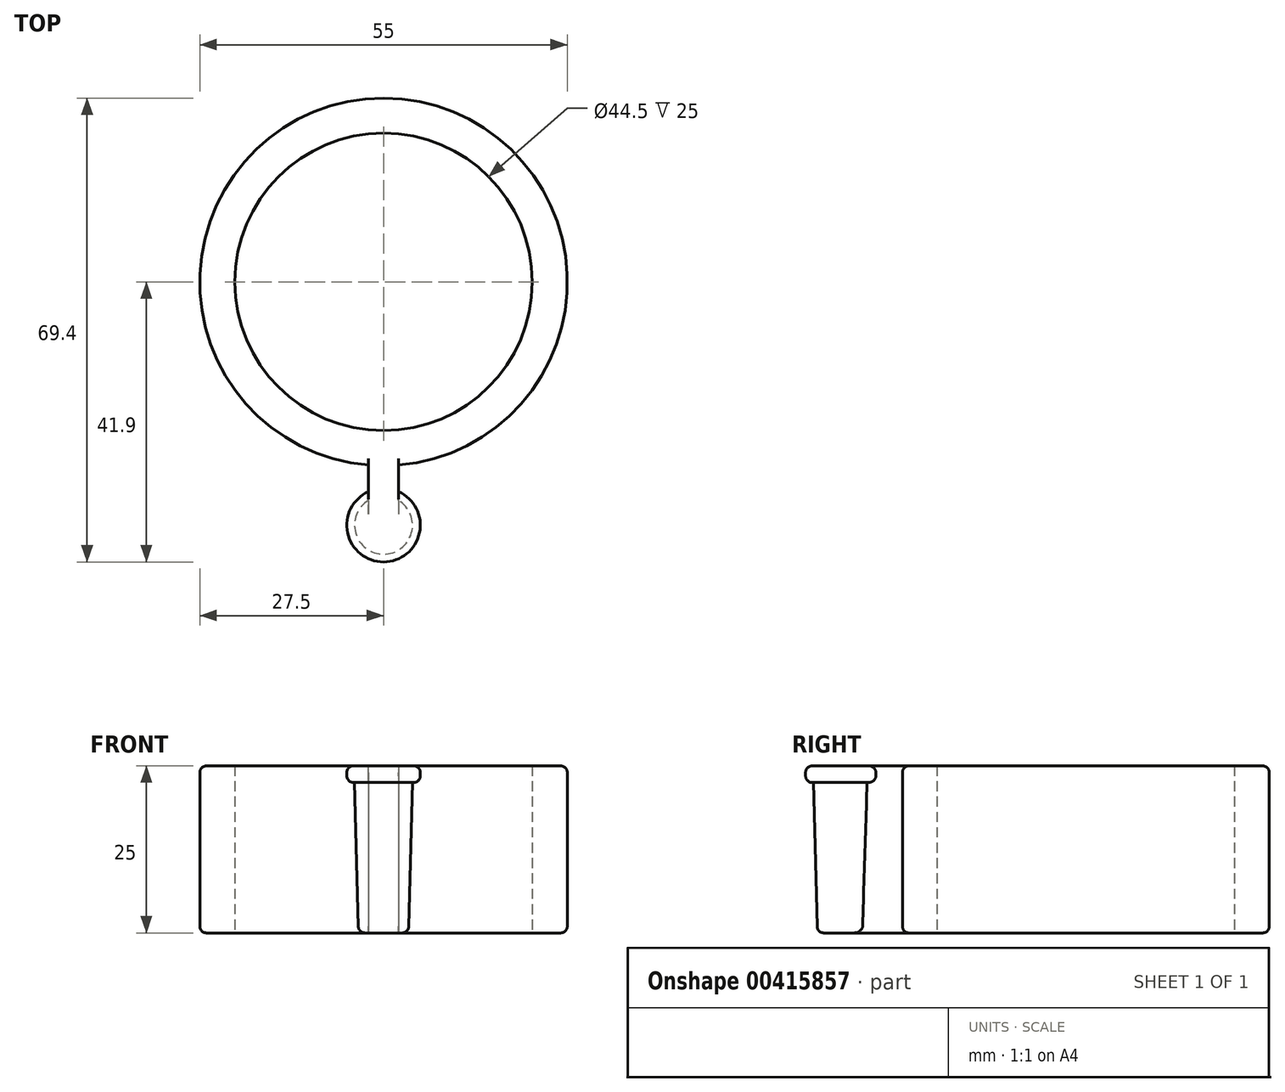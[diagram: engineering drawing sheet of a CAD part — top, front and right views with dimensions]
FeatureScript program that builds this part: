
annotation { "Feature Type Name" : "Feature", "Feature Type Description" : "" }
export const myFeature = defineFeature(function(context is Context, id is Id, definition is map)
    precondition{}
    {
        {
            var Q0;
            Q0=qCreatedBy(makeId("Top.planeOp"),FACE);
            var sketch = newSketch(context, id + "F0", { "sketchPlane" : qUnion([Q0])});
            skCircle(sketch, "E0", {"center": v(0, 0) * mm, "radius": 27.5 * mm});
            skCircle(sketch, "E1", {"center": v(0, 0) * mm, "radius": 22.25 * mm});
            skSolve(sketch);
        }
        {
            var Q0;
            Q0=makeQuery(id+"F0.imprint","IMPRINT",FACE,{"disambiguationData":[TD([[makeQuery(id+"F0.imprint","IMPRINT",EDGE,{"derivedFrom":sQuery(id+"F0.wireOp",EDGE,"G8LjAgH3-xLvY-zyrB-EcI2-Q5GBPlgTxXza")}),-1.0]])]});
            var Q1;
            Q1=makeQuery(id+"F0.imprint","IMPRINT",FACE,{"disambiguationData":[TD([[makeQuery(id+"F0.imprint","IMPRINT",EDGE,{"derivedFrom":sQuery(id+"F0.wireOp",EDGE,"E0")}),1.0]])]});
            extrude(context, id + "F1", {"entities" : qUnion([Q0, Q1]), "depth" : 25 * mm});
        }
        {
            var Q0;
            Q0=qCreatedBy(makeId("Right.planeOp"),FACE);
            var sketch = newSketch(context, id + "F2", { "sketchPlane" : qUnion([Q0])});
            skLineSegment(sketch, "E2.0", {"start": v(-2.25, 25) * mm, "end": v(2.25, 25) * mm});
            skLineSegment(sketch, "E3", {"start": v(2.25, 25) * mm, "end": v(2.25, 0) * mm});
            skLineSegment(sketch, "E4", {"start": v(-2.25, 25) * mm, "end": v(-2.25, 0) * mm});
            skPoint(sketch, "E5.orphan", {"position": v(-27.5, 25) * mm});
            skPoint(sketch, "E6.orphan", {"position": v(27.5, 25) * mm});
            skLineSegment(sketch, "E7", {"start": v(2.25, 0) * mm, "end": v(-2.25, 0) * mm});
            skSolve(sketch);
        }
        {
            var Q0;
            Q0=qCreatedBy(makeId("Front.planeOp"),FACE);
            cPlane(context, id + "F3", {"entities" : qUnion([Q0]), "cplaneType" : CPlaneType.OFFSET, "offset" : ((55 / 2) + 8) * mm, "width" : 150 * mm, "height" : 150 * mm});
        }
        {
            var Q0;
            Q0=qCreatedBy(id+"F3.planeOp",FACE);
            var sketch = newSketch(context, id + "F4", { "sketchPlane" : qUnion([Q0])});
            skLineSegment(sketch, "E8.0", {"start": v(-2.25, 25) * mm, "end": v(2.25, 25) * mm});
            skLineSegment(sketch, "E9", {"start": v(2.25, 25) * mm, "end": v(2.25, 0) * mm});
            skLineSegment(sketch, "E10", {"start": v(-2.25, 25) * mm, "end": v(-2.25, 0) * mm});
            skPoint(sketch, "E11.orphan", {"position": v(-27.5, 25) * mm});
            skPoint(sketch, "E12.orphan", {"position": v(27.5, 25) * mm});
            skLineSegment(sketch, "E13", {"start": v(2.25, 0) * mm, "end": v(-2.25, 0) * mm});
            skSolve(sketch);
        }
        {
            var Q0;
            Q0=makeQuery(id+"F8.boolean.opBoolean","MERGE",FACE,{"derivedFrom":[makeQuery(id+"F1.opExtrude","CAP_FACE",FACE,{"disambiguationData":[OSD([sQuery(id+"F0.wireOp",EDGE,"G8LjAgH3-xLvY-zyrB-EcI2-Q5GBPlgTxXza"),sQuery(id+"F0.wireOp",EDGE,"TrwqLrFX-PL90-re9a-MtEJ-rmMyrkPkawyX"),sQuery(id+"F0.wireOp",EDGE,"UjxkqwY4-PdTA-AksG-SiQF-jZbG1BaBsUn5"),sQuery(id+"F0.wireOp",EDGE,"fVokzXBM-DoVm-PEKz-oAMV-pJyANEdUcLKx"),sQuery(id+"F0.wireOp",EDGE,"49fcca35-5327-4fc4-9edf-febdfafce598.1.0"),sQuery(id+"F0.wireOp",EDGE,"49fcca35-5327-4fc4-9edf-febdfafce598.1.1"),sQuery(id+"F0.wireOp",EDGE,"49fcca35-5327-4fc4-9edf-febdfafce598.2.0"),sQuery(id+"F0.wireOp",EDGE,"49fcca35-5327-4fc4-9edf-febdfafce598.2.1"),sQuery(id+"F0.wireOp",EDGE,"49fcca35-5327-4fc4-9edf-febdfafce598.3.0"),sQuery(id+"F0.wireOp",EDGE,"49fcca35-5327-4fc4-9edf-febdfafce598.3.1"),sQuery(id+"F0.wireOp",EDGE,"49fcca35-5327-4fc4-9edf-febdfafce598.4.0"),sQuery(id+"F0.wireOp",EDGE,"49fcca35-5327-4fc4-9edf-febdfafce598.4.1"),sQuery(id+"F0.wireOp",EDGE,"49fcca35-5327-4fc4-9edf-febdfafce598.5.0"),sQuery(id+"F0.wireOp",EDGE,"49fcca35-5327-4fc4-9edf-febdfafce598.5.1"),sQuery(id+"F0.wireOp",EDGE,"49fcca35-5327-4fc4-9edf-febdfafce598.6.0"),sQuery(id+"F0.wireOp",EDGE,"49fcca35-5327-4fc4-9edf-febdfafce598.6.1"),sQuery(id+"F0.wireOp",EDGE,"49fcca35-5327-4fc4-9edf-febdfafce598.7.0"),sQuery(id+"F0.wireOp",EDGE,"49fcca35-5327-4fc4-9edf-febdfafce598.7.1"),sQuery(id+"F0.wireOp",EDGE,"49fcca35-5327-4fc4-9edf-febdfafce598.8.0"),sQuery(id+"F0.wireOp",EDGE,"49fcca35-5327-4fc4-9edf-febdfafce598.8.1"),sQuery(id+"F0.wireOp",EDGE,"49fcca35-5327-4fc4-9edf-febdfafce598.9.0"),sQuery(id+"F0.wireOp",EDGE,"49fcca35-5327-4fc4-9edf-febdfafce598.9.1"),sQuery(id+"F0.wireOp",EDGE,"49fcca35-5327-4fc4-9edf-febdfafce598.10.0"),sQuery(id+"F0.wireOp",EDGE,"49fcca35-5327-4fc4-9edf-febdfafce598.10.1"),sQuery(id+"F0.wireOp",EDGE,"49fcca35-5327-4fc4-9edf-febdfafce598.11.0"),sQuery(id+"F0.wireOp",EDGE,"49fcca35-5327-4fc4-9edf-febdfafce598.11.1"),sQuery(id+"F0.wireOp",EDGE,"E0"),sQuery(id+"F0.wireOp",EDGE,"186aa438-9647-4cfe-b0f9-6be8f9764cad.trimOffspring"),sQuery(id+"F0.wireOp",EDGE,"58acbb79-e031-4346-80cd-8f142c05cd66.trimOffspring"),sQuery(id+"F0.wireOp",EDGE,"3233a842-d643-44c9-9bbf-ea4239158afc.trimOffspring"),sQuery(id+"F0.wireOp",EDGE,"f7f68b4e-f9ab-4057-8afc-ee08b94aada7.trimOffspring"),sQuery(id+"F0.wireOp",EDGE,"09b310b1-5268-4a26-a1f0-9bfda1f777f2.trimOffspring"),sQuery(id+"F0.wireOp",EDGE,"060726c4-0cf8-4064-904b-376d507987ac.trimOffspring"),sQuery(id+"F0.wireOp",EDGE,"7db7c674-86fd-48a5-aafa-5ef47b045ad1.trimOffspring"),sQuery(id+"F0.wireOp",EDGE,"ee3f2828-a48d-4b0c-ae87-b5a3684aa839.trimOffspring"),sQuery(id+"F0.wireOp",EDGE,"121f7678-b1ac-4d92-82c7-cca3d9a6b96b.trimOffspring"),sQuery(id+"F0.wireOp",EDGE,"3299b9a4-9380-4aca-859c-d639b934480d.trimOffspring"),sQuery(id+"F0.wireOp",EDGE,"b3303ed2-3daa-417e-bc2a-0f817123942c.trimOffspring"),sQuery(id+"F0.wireOp",EDGE,"a895326a-27a2-4a7e-8581-99855a22d4ec.trimOffspring"),sQuery(id+"F0.wireOp",EDGE,"c02cc152-68c9-4426-bdff-746dfd7627e0.trimOffspring"),sQuery(id+"F0.wireOp",EDGE,"6c8ed3d3-5cf9-4a29-b357-0998a04bb589.trimOffspring"),sQuery(id+"F0.wireOp",EDGE,"684efb0c-3531-44ac-83f3-1a78a4206dcb.trimOffspring"),sQuery(id+"F0.wireOp",EDGE,"eba51431-7082-4955-99c3-f2a0537aa775.trimOffspring"),sQuery(id+"F0.wireOp",EDGE,"16738435-4d55-46a7-bca6-1884286cbfd4.trimOffspring"),sQuery(id+"F0.wireOp",EDGE,"9c81e3d0-4d59-40e4-9b67-e092ea49d70e.trimOffspring"),sQuery(id+"F0.wireOp",EDGE,"baf1dc81-3dee-4657-96dd-312042d0ee18.trimOffspring"),sQuery(id+"F0.wireOp",EDGE,"007a2b50-8cc2-4d21-b63f-0f999ab53aaa.trimOffspring"),sQuery(id+"F0.wireOp",EDGE,"d51a5eac-9464-4b9c-9b0a-bc628fde9c98.trimOffspring"),sQuery(id+"F0.wireOp",EDGE,"2bc9f3e7-df2b-4828-93b8-591f512d2fb0.trimOffspring")])],"isStart":false}),makeQuery(id+"F8.opExtrude","SWEPT_FACE",FACE,{"disambiguationData":[OSD([sQuery(id+"F4.wireOp",EDGE,"E8.0")])]})]});
            var sketch = newSketch(context, id + "F5", { "sketchPlane" : qUnion([Q0])});
            skCircle(sketch, "E14", {"center": v(0, -36.4) * mm, "radius": 4.4 * mm});
            skPoint(sketch, "E14.first.point", {"position": v(0, -32) * mm});
            skPoint(sketch, "E14.second.point", {"position": v(-3.9, -38.43) * mm});
            skPoint(sketch, "E14.third.point", {"position": v(2.2, -40.2) * mm});
            skSolve(sketch);
        }
        {
            var Q0;
            Q0=makeQuery(id+"F8.boolean.opBoolean","MERGE",FACE,{"derivedFrom":[makeQuery(id+"F1.opExtrude","CAP_FACE",FACE,{"disambiguationData":[OSD([sQuery(id+"F0.wireOp",EDGE,"G8LjAgH3-xLvY-zyrB-EcI2-Q5GBPlgTxXza"),sQuery(id+"F0.wireOp",EDGE,"TrwqLrFX-PL90-re9a-MtEJ-rmMyrkPkawyX"),sQuery(id+"F0.wireOp",EDGE,"UjxkqwY4-PdTA-AksG-SiQF-jZbG1BaBsUn5"),sQuery(id+"F0.wireOp",EDGE,"fVokzXBM-DoVm-PEKz-oAMV-pJyANEdUcLKx"),sQuery(id+"F0.wireOp",EDGE,"49fcca35-5327-4fc4-9edf-febdfafce598.1.0"),sQuery(id+"F0.wireOp",EDGE,"49fcca35-5327-4fc4-9edf-febdfafce598.1.1"),sQuery(id+"F0.wireOp",EDGE,"49fcca35-5327-4fc4-9edf-febdfafce598.2.0"),sQuery(id+"F0.wireOp",EDGE,"49fcca35-5327-4fc4-9edf-febdfafce598.2.1"),sQuery(id+"F0.wireOp",EDGE,"49fcca35-5327-4fc4-9edf-febdfafce598.3.0"),sQuery(id+"F0.wireOp",EDGE,"49fcca35-5327-4fc4-9edf-febdfafce598.3.1"),sQuery(id+"F0.wireOp",EDGE,"49fcca35-5327-4fc4-9edf-febdfafce598.4.0"),sQuery(id+"F0.wireOp",EDGE,"49fcca35-5327-4fc4-9edf-febdfafce598.4.1"),sQuery(id+"F0.wireOp",EDGE,"49fcca35-5327-4fc4-9edf-febdfafce598.5.0"),sQuery(id+"F0.wireOp",EDGE,"49fcca35-5327-4fc4-9edf-febdfafce598.5.1"),sQuery(id+"F0.wireOp",EDGE,"49fcca35-5327-4fc4-9edf-febdfafce598.6.0"),sQuery(id+"F0.wireOp",EDGE,"49fcca35-5327-4fc4-9edf-febdfafce598.6.1"),sQuery(id+"F0.wireOp",EDGE,"49fcca35-5327-4fc4-9edf-febdfafce598.7.0"),sQuery(id+"F0.wireOp",EDGE,"49fcca35-5327-4fc4-9edf-febdfafce598.7.1"),sQuery(id+"F0.wireOp",EDGE,"49fcca35-5327-4fc4-9edf-febdfafce598.8.0"),sQuery(id+"F0.wireOp",EDGE,"49fcca35-5327-4fc4-9edf-febdfafce598.8.1"),sQuery(id+"F0.wireOp",EDGE,"49fcca35-5327-4fc4-9edf-febdfafce598.9.0"),sQuery(id+"F0.wireOp",EDGE,"49fcca35-5327-4fc4-9edf-febdfafce598.9.1"),sQuery(id+"F0.wireOp",EDGE,"49fcca35-5327-4fc4-9edf-febdfafce598.10.0"),sQuery(id+"F0.wireOp",EDGE,"49fcca35-5327-4fc4-9edf-febdfafce598.10.1"),sQuery(id+"F0.wireOp",EDGE,"49fcca35-5327-4fc4-9edf-febdfafce598.11.0"),sQuery(id+"F0.wireOp",EDGE,"49fcca35-5327-4fc4-9edf-febdfafce598.11.1"),sQuery(id+"F0.wireOp",EDGE,"E0"),sQuery(id+"F0.wireOp",EDGE,"186aa438-9647-4cfe-b0f9-6be8f9764cad.trimOffspring"),sQuery(id+"F0.wireOp",EDGE,"58acbb79-e031-4346-80cd-8f142c05cd66.trimOffspring"),sQuery(id+"F0.wireOp",EDGE,"3233a842-d643-44c9-9bbf-ea4239158afc.trimOffspring"),sQuery(id+"F0.wireOp",EDGE,"f7f68b4e-f9ab-4057-8afc-ee08b94aada7.trimOffspring"),sQuery(id+"F0.wireOp",EDGE,"09b310b1-5268-4a26-a1f0-9bfda1f777f2.trimOffspring"),sQuery(id+"F0.wireOp",EDGE,"060726c4-0cf8-4064-904b-376d507987ac.trimOffspring"),sQuery(id+"F0.wireOp",EDGE,"7db7c674-86fd-48a5-aafa-5ef47b045ad1.trimOffspring"),sQuery(id+"F0.wireOp",EDGE,"ee3f2828-a48d-4b0c-ae87-b5a3684aa839.trimOffspring"),sQuery(id+"F0.wireOp",EDGE,"121f7678-b1ac-4d92-82c7-cca3d9a6b96b.trimOffspring"),sQuery(id+"F0.wireOp",EDGE,"3299b9a4-9380-4aca-859c-d639b934480d.trimOffspring"),sQuery(id+"F0.wireOp",EDGE,"b3303ed2-3daa-417e-bc2a-0f817123942c.trimOffspring"),sQuery(id+"F0.wireOp",EDGE,"a895326a-27a2-4a7e-8581-99855a22d4ec.trimOffspring"),sQuery(id+"F0.wireOp",EDGE,"c02cc152-68c9-4426-bdff-746dfd7627e0.trimOffspring"),sQuery(id+"F0.wireOp",EDGE,"6c8ed3d3-5cf9-4a29-b357-0998a04bb589.trimOffspring"),sQuery(id+"F0.wireOp",EDGE,"684efb0c-3531-44ac-83f3-1a78a4206dcb.trimOffspring"),sQuery(id+"F0.wireOp",EDGE,"eba51431-7082-4955-99c3-f2a0537aa775.trimOffspring"),sQuery(id+"F0.wireOp",EDGE,"16738435-4d55-46a7-bca6-1884286cbfd4.trimOffspring"),sQuery(id+"F0.wireOp",EDGE,"9c81e3d0-4d59-40e4-9b67-e092ea49d70e.trimOffspring"),sQuery(id+"F0.wireOp",EDGE,"baf1dc81-3dee-4657-96dd-312042d0ee18.trimOffspring"),sQuery(id+"F0.wireOp",EDGE,"007a2b50-8cc2-4d21-b63f-0f999ab53aaa.trimOffspring"),sQuery(id+"F0.wireOp",EDGE,"d51a5eac-9464-4b9c-9b0a-bc628fde9c98.trimOffspring"),sQuery(id+"F0.wireOp",EDGE,"2bc9f3e7-df2b-4828-93b8-591f512d2fb0.trimOffspring")])],"isStart":true}),makeQuery(id+"F8.opExtrude","SWEPT_FACE",FACE,{"disambiguationData":[OSD([sQuery(id+"F4.wireOp",EDGE,"E13")])]})]});
            var sketch = newSketch(context, id + "F6", { "sketchPlane" : qUnion([Q0])});
            skCircle(sketch, "E15.0", {"center": v(0, 36.4) * mm, "radius": 4.4 * mm});
            skCircle(sketch, "E16", {"center": v(0, 36.4) * mm, "radius": 3.75 * mm});
            skSolve(sketch);
        }
        {
            var Q0;
            Q0=makeQuery(id+"F5.imprint","IMPRINT",FACE,{"disambiguationData":[TD([[makeQuery(id+"F5.imprint","IMPRINT",EDGE,{"derivedFrom":sQuery(id+"F5.wireOp",EDGE,"E14")}),1.0]])]});
            var Q1;
            Q1=makeQuery(id+"F6.imprint","IMPRINT",FACE,{"disambiguationData":[TD([[makeQuery(id+"F6.imprint","IMPRINT",EDGE,{"derivedFrom":sQuery(id+"F6.wireOp",EDGE,"E16")}),1.0]])]});
            loft(context, id + "F7", {"sheetProfilesArray" : [{ "sheetProfileEntities" : qUnion([Q0]) }, { "sheetProfileEntities" : qUnion([Q1]) }]});
        }
        {
            var Q0;
            Q0=makeQuery(id+"F4.imprint","IMPRINT",FACE,{"disambiguationData":[TD([[makeQuery(id+"F4.imprint","IMPRINT",EDGE,{"derivedFrom":sQuery(id+"F4.wireOp",EDGE,"E8.0")}),-1.0]])]});
            var Q1;
            Q1=makeQuery(id+"F1.opExtrude","SWEPT_BODY",BODY,{"disambiguationData":[OSD([sQuery(id+"F0.wireOp",EDGE,"G8LjAgH3-xLvY-zyrB-EcI2-Q5GBPlgTxXza"),sQuery(id+"F0.wireOp",EDGE,"TrwqLrFX-PL90-re9a-MtEJ-rmMyrkPkawyX"),sQuery(id+"F0.wireOp",EDGE,"UjxkqwY4-PdTA-AksG-SiQF-jZbG1BaBsUn5"),sQuery(id+"F0.wireOp",EDGE,"fVokzXBM-DoVm-PEKz-oAMV-pJyANEdUcLKx"),sQuery(id+"F0.wireOp",EDGE,"49fcca35-5327-4fc4-9edf-febdfafce598.1.0"),sQuery(id+"F0.wireOp",EDGE,"49fcca35-5327-4fc4-9edf-febdfafce598.1.1"),sQuery(id+"F0.wireOp",EDGE,"49fcca35-5327-4fc4-9edf-febdfafce598.2.0"),sQuery(id+"F0.wireOp",EDGE,"49fcca35-5327-4fc4-9edf-febdfafce598.2.1"),sQuery(id+"F0.wireOp",EDGE,"49fcca35-5327-4fc4-9edf-febdfafce598.3.0"),sQuery(id+"F0.wireOp",EDGE,"49fcca35-5327-4fc4-9edf-febdfafce598.3.1"),sQuery(id+"F0.wireOp",EDGE,"49fcca35-5327-4fc4-9edf-febdfafce598.4.0"),sQuery(id+"F0.wireOp",EDGE,"49fcca35-5327-4fc4-9edf-febdfafce598.4.1"),sQuery(id+"F0.wireOp",EDGE,"49fcca35-5327-4fc4-9edf-febdfafce598.5.0"),sQuery(id+"F0.wireOp",EDGE,"49fcca35-5327-4fc4-9edf-febdfafce598.5.1"),sQuery(id+"F0.wireOp",EDGE,"49fcca35-5327-4fc4-9edf-febdfafce598.6.0"),sQuery(id+"F0.wireOp",EDGE,"49fcca35-5327-4fc4-9edf-febdfafce598.6.1"),sQuery(id+"F0.wireOp",EDGE,"49fcca35-5327-4fc4-9edf-febdfafce598.7.0"),sQuery(id+"F0.wireOp",EDGE,"49fcca35-5327-4fc4-9edf-febdfafce598.7.1"),sQuery(id+"F0.wireOp",EDGE,"49fcca35-5327-4fc4-9edf-febdfafce598.8.0"),sQuery(id+"F0.wireOp",EDGE,"49fcca35-5327-4fc4-9edf-febdfafce598.8.1"),sQuery(id+"F0.wireOp",EDGE,"49fcca35-5327-4fc4-9edf-febdfafce598.9.0"),sQuery(id+"F0.wireOp",EDGE,"49fcca35-5327-4fc4-9edf-febdfafce598.9.1"),sQuery(id+"F0.wireOp",EDGE,"49fcca35-5327-4fc4-9edf-febdfafce598.10.0"),sQuery(id+"F0.wireOp",EDGE,"49fcca35-5327-4fc4-9edf-febdfafce598.10.1"),sQuery(id+"F0.wireOp",EDGE,"49fcca35-5327-4fc4-9edf-febdfafce598.11.0"),sQuery(id+"F0.wireOp",EDGE,"49fcca35-5327-4fc4-9edf-febdfafce598.11.1"),sQuery(id+"F0.wireOp",EDGE,"E0"),sQuery(id+"F0.wireOp",EDGE,"186aa438-9647-4cfe-b0f9-6be8f9764cad.trimOffspring"),sQuery(id+"F0.wireOp",EDGE,"58acbb79-e031-4346-80cd-8f142c05cd66.trimOffspring"),sQuery(id+"F0.wireOp",EDGE,"3233a842-d643-44c9-9bbf-ea4239158afc.trimOffspring"),sQuery(id+"F0.wireOp",EDGE,"f7f68b4e-f9ab-4057-8afc-ee08b94aada7.trimOffspring"),sQuery(id+"F0.wireOp",EDGE,"09b310b1-5268-4a26-a1f0-9bfda1f777f2.trimOffspring"),sQuery(id+"F0.wireOp",EDGE,"060726c4-0cf8-4064-904b-376d507987ac.trimOffspring"),sQuery(id+"F0.wireOp",EDGE,"7db7c674-86fd-48a5-aafa-5ef47b045ad1.trimOffspring"),sQuery(id+"F0.wireOp",EDGE,"ee3f2828-a48d-4b0c-ae87-b5a3684aa839.trimOffspring"),sQuery(id+"F0.wireOp",EDGE,"121f7678-b1ac-4d92-82c7-cca3d9a6b96b.trimOffspring"),sQuery(id+"F0.wireOp",EDGE,"3299b9a4-9380-4aca-859c-d639b934480d.trimOffspring"),sQuery(id+"F0.wireOp",EDGE,"b3303ed2-3daa-417e-bc2a-0f817123942c.trimOffspring"),sQuery(id+"F0.wireOp",EDGE,"a895326a-27a2-4a7e-8581-99855a22d4ec.trimOffspring"),sQuery(id+"F0.wireOp",EDGE,"c02cc152-68c9-4426-bdff-746dfd7627e0.trimOffspring"),sQuery(id+"F0.wireOp",EDGE,"6c8ed3d3-5cf9-4a29-b357-0998a04bb589.trimOffspring"),sQuery(id+"F0.wireOp",EDGE,"684efb0c-3531-44ac-83f3-1a78a4206dcb.trimOffspring"),sQuery(id+"F0.wireOp",EDGE,"eba51431-7082-4955-99c3-f2a0537aa775.trimOffspring"),sQuery(id+"F0.wireOp",EDGE,"16738435-4d55-46a7-bca6-1884286cbfd4.trimOffspring"),sQuery(id+"F0.wireOp",EDGE,"9c81e3d0-4d59-40e4-9b67-e092ea49d70e.trimOffspring"),sQuery(id+"F0.wireOp",EDGE,"baf1dc81-3dee-4657-96dd-312042d0ee18.trimOffspring"),sQuery(id+"F0.wireOp",EDGE,"007a2b50-8cc2-4d21-b63f-0f999ab53aaa.trimOffspring"),sQuery(id+"F0.wireOp",EDGE,"d51a5eac-9464-4b9c-9b0a-bc628fde9c98.trimOffspring"),sQuery(id+"F0.wireOp",EDGE,"2bc9f3e7-df2b-4828-93b8-591f512d2fb0.trimOffspring")])]});
            var Q2;
            Q2=makeQuery(id+"F7.opLoft","SWEPT_BODY",BODY,{"disambiguationData":[OSD([makeQuery(id+"F5.imprint","IMPRINT",FACE,{"disambiguationData":[TD([[makeQuery(id+"F5.imprint","IMPRINT",EDGE,{"derivedFrom":sQuery(id+"F5.wireOp",EDGE,"E14")}),1.0]])]}),makeQuery(id+"F6.imprint","IMPRINT",FACE,{"disambiguationData":[TD([[makeQuery(id+"F6.imprint","IMPRINT",EDGE,{"derivedFrom":sQuery(id+"F6.wireOp",EDGE,"E16")}),1.0]])]})])]});
            extrude(context, id + "F8", {"entities" : qUnion([Q0]), "operationType" : NewBodyOperationType.ADD, "endBound" : BoundingType.UP_TO_BODY, "oppositeDirection" : true, "endBoundEntityBody" : qUnion([Q1]), "depth" : 25 * mm, "hasSecondDirection" : true, "secondDirectionBound" : SecondDirectionBoundingType.UP_TO_BODY, "secondDirectionOppositeDirection" : true, "secondDirectionBoundEntityBody" : qUnion([Q2]), "secondDirectionDepth" : 25 * mm});
        }
        {
            var Q0;
            Q0=makeQuery(id+"F8.boolean.opBoolean","MERGE",FACE,{"derivedFrom":[makeQuery(id+"F1.opExtrude","CAP_FACE",FACE,{"disambiguationData":[OSD([sQuery(id+"F0.wireOp",EDGE,"G8LjAgH3-xLvY-zyrB-EcI2-Q5GBPlgTxXza"),sQuery(id+"F0.wireOp",EDGE,"TrwqLrFX-PL90-re9a-MtEJ-rmMyrkPkawyX"),sQuery(id+"F0.wireOp",EDGE,"UjxkqwY4-PdTA-AksG-SiQF-jZbG1BaBsUn5"),sQuery(id+"F0.wireOp",EDGE,"fVokzXBM-DoVm-PEKz-oAMV-pJyANEdUcLKx"),sQuery(id+"F0.wireOp",EDGE,"49fcca35-5327-4fc4-9edf-febdfafce598.1.0"),sQuery(id+"F0.wireOp",EDGE,"49fcca35-5327-4fc4-9edf-febdfafce598.1.1"),sQuery(id+"F0.wireOp",EDGE,"49fcca35-5327-4fc4-9edf-febdfafce598.2.0"),sQuery(id+"F0.wireOp",EDGE,"49fcca35-5327-4fc4-9edf-febdfafce598.2.1"),sQuery(id+"F0.wireOp",EDGE,"49fcca35-5327-4fc4-9edf-febdfafce598.3.0"),sQuery(id+"F0.wireOp",EDGE,"49fcca35-5327-4fc4-9edf-febdfafce598.3.1"),sQuery(id+"F0.wireOp",EDGE,"49fcca35-5327-4fc4-9edf-febdfafce598.4.0"),sQuery(id+"F0.wireOp",EDGE,"49fcca35-5327-4fc4-9edf-febdfafce598.4.1"),sQuery(id+"F0.wireOp",EDGE,"49fcca35-5327-4fc4-9edf-febdfafce598.5.0"),sQuery(id+"F0.wireOp",EDGE,"49fcca35-5327-4fc4-9edf-febdfafce598.5.1"),sQuery(id+"F0.wireOp",EDGE,"49fcca35-5327-4fc4-9edf-febdfafce598.6.0"),sQuery(id+"F0.wireOp",EDGE,"49fcca35-5327-4fc4-9edf-febdfafce598.6.1"),sQuery(id+"F0.wireOp",EDGE,"49fcca35-5327-4fc4-9edf-febdfafce598.7.0"),sQuery(id+"F0.wireOp",EDGE,"49fcca35-5327-4fc4-9edf-febdfafce598.7.1"),sQuery(id+"F0.wireOp",EDGE,"49fcca35-5327-4fc4-9edf-febdfafce598.8.0"),sQuery(id+"F0.wireOp",EDGE,"49fcca35-5327-4fc4-9edf-febdfafce598.8.1"),sQuery(id+"F0.wireOp",EDGE,"49fcca35-5327-4fc4-9edf-febdfafce598.9.0"),sQuery(id+"F0.wireOp",EDGE,"49fcca35-5327-4fc4-9edf-febdfafce598.9.1"),sQuery(id+"F0.wireOp",EDGE,"49fcca35-5327-4fc4-9edf-febdfafce598.10.0"),sQuery(id+"F0.wireOp",EDGE,"49fcca35-5327-4fc4-9edf-febdfafce598.10.1"),sQuery(id+"F0.wireOp",EDGE,"49fcca35-5327-4fc4-9edf-febdfafce598.11.0"),sQuery(id+"F0.wireOp",EDGE,"49fcca35-5327-4fc4-9edf-febdfafce598.11.1"),sQuery(id+"F0.wireOp",EDGE,"E0"),sQuery(id+"F0.wireOp",EDGE,"186aa438-9647-4cfe-b0f9-6be8f9764cad.trimOffspring"),sQuery(id+"F0.wireOp",EDGE,"58acbb79-e031-4346-80cd-8f142c05cd66.trimOffspring"),sQuery(id+"F0.wireOp",EDGE,"3233a842-d643-44c9-9bbf-ea4239158afc.trimOffspring"),sQuery(id+"F0.wireOp",EDGE,"f7f68b4e-f9ab-4057-8afc-ee08b94aada7.trimOffspring"),sQuery(id+"F0.wireOp",EDGE,"09b310b1-5268-4a26-a1f0-9bfda1f777f2.trimOffspring"),sQuery(id+"F0.wireOp",EDGE,"060726c4-0cf8-4064-904b-376d507987ac.trimOffspring"),sQuery(id+"F0.wireOp",EDGE,"7db7c674-86fd-48a5-aafa-5ef47b045ad1.trimOffspring"),sQuery(id+"F0.wireOp",EDGE,"ee3f2828-a48d-4b0c-ae87-b5a3684aa839.trimOffspring"),sQuery(id+"F0.wireOp",EDGE,"121f7678-b1ac-4d92-82c7-cca3d9a6b96b.trimOffspring"),sQuery(id+"F0.wireOp",EDGE,"3299b9a4-9380-4aca-859c-d639b934480d.trimOffspring"),sQuery(id+"F0.wireOp",EDGE,"b3303ed2-3daa-417e-bc2a-0f817123942c.trimOffspring"),sQuery(id+"F0.wireOp",EDGE,"a895326a-27a2-4a7e-8581-99855a22d4ec.trimOffspring"),sQuery(id+"F0.wireOp",EDGE,"c02cc152-68c9-4426-bdff-746dfd7627e0.trimOffspring"),sQuery(id+"F0.wireOp",EDGE,"6c8ed3d3-5cf9-4a29-b357-0998a04bb589.trimOffspring"),sQuery(id+"F0.wireOp",EDGE,"684efb0c-3531-44ac-83f3-1a78a4206dcb.trimOffspring"),sQuery(id+"F0.wireOp",EDGE,"eba51431-7082-4955-99c3-f2a0537aa775.trimOffspring"),sQuery(id+"F0.wireOp",EDGE,"16738435-4d55-46a7-bca6-1884286cbfd4.trimOffspring"),sQuery(id+"F0.wireOp",EDGE,"9c81e3d0-4d59-40e4-9b67-e092ea49d70e.trimOffspring"),sQuery(id+"F0.wireOp",EDGE,"baf1dc81-3dee-4657-96dd-312042d0ee18.trimOffspring"),sQuery(id+"F0.wireOp",EDGE,"007a2b50-8cc2-4d21-b63f-0f999ab53aaa.trimOffspring"),sQuery(id+"F0.wireOp",EDGE,"d51a5eac-9464-4b9c-9b0a-bc628fde9c98.trimOffspring"),sQuery(id+"F0.wireOp",EDGE,"2bc9f3e7-df2b-4828-93b8-591f512d2fb0.trimOffspring")])],"isStart":false}),makeQuery(id+"F7.opLoft","CAP_FACE",FACE,{"disambiguationData":[OSD([makeQuery(id+"F5.imprint","IMPRINT",FACE,{"disambiguationData":[TD([[makeQuery(id+"F5.imprint","IMPRINT",EDGE,{"derivedFrom":sQuery(id+"F5.wireOp",EDGE,"E14")}),1.0]])]})])],"isStart":true}),makeQuery(id+"F8.opExtrude","SWEPT_FACE",FACE,{"disambiguationData":[OSD([sQuery(id+"F4.wireOp",EDGE,"E8.0")])]})]});
            var sketch = newSketch(context, id + "F9", { "sketchPlane" : qUnion([Q0])});
            skCircle(sketch, "E17", {"center": v(0, -36.4) * mm, "radius": 5.5 * mm});
            skSolve(sketch);
        }
        {
            var Q0;
            {var subQ6=makeQuery(id+"F7.opLoft","MID_CAP_EDGE",EDGE,{"disambiguationData":[OSD([sQuery(id+"F5.wireOp",EDGE,"E14")])],"capPos":0.0});Q0=makeQuery(id+"F9.imprint","IMPRINT",FACE,{"disambiguationData":[TD([[makeQuery(id+"F9.imprint","IMPRINT",EDGE,{"derivedFrom":subQ6}),1.0]])]});}
            var Q1;
            {var subQ6=makeQuery(id+"F7.opLoft","MID_CAP_EDGE",EDGE,{"disambiguationData":[OSD([sQuery(id+"F5.wireOp",EDGE,"E14")])],"capPos":0.0});Q1=makeQuery(id+"F9.imprint","IMPRINT",FACE,{"disambiguationData":[TD([[makeQuery(id+"F9.imprint","IMPRINT",EDGE,{"derivedFrom":subQ6}),-1.0]])]});}
            extrude(context, id + "F10", {"entities" : qUnion([Q0, Q1]), "operationType" : NewBodyOperationType.ADD, "oppositeDirection" : true, "depth" : 2.5 * mm});
        }
        {
            var Q0;
            Q0=makeQuery(id+"F8.opExtrude","TWEAK_EDGE",EDGE,{"derivedFrom":[makeQuery(id+"F4.imprint","IMPRINT",EDGE,{"derivedFrom":sQuery(id+"F4.wireOp",EDGE,"E8.0")}),makeQuery(id+"F4.imprint","IMPRINT",EDGE,{"derivedFrom":sQuery(id+"F4.wireOp",EDGE,"E9")})]});
            var Q1;
            Q1=makeQuery(id+"F8.opExtrude","TWEAK_EDGE",EDGE,{"derivedFrom":[makeQuery(id+"F4.imprint","IMPRINT",EDGE,{"derivedFrom":sQuery(id+"F4.wireOp",EDGE,"E8.0")}),makeQuery(id+"F4.imprint","IMPRINT",EDGE,{"derivedFrom":sQuery(id+"F4.wireOp",EDGE,"E10")})]});
            var Q2;
            Q2=makeQuery(id+"F10.opExtrude","CAP_EDGE",EDGE,{"disambiguationData":[OSD([sQuery(id+"F9.wireOp",EDGE,"E17")])],"isStart":true});
            var Q3;
            Q3=makeQuery(id+"F1.opExtrude","CAP_EDGE",EDGE,{"disambiguationData":[OSD([sQuery(id+"F0.wireOp",EDGE,"E0")])],"isStart":false});
            fillet(context, id + "F11", {"entities" : qUnion([Q0, Q1, Q2, Q3]), "radius" : 1 * mm, "tangentPropagation" : true, "allowEdgeOverflow" : false});
        }
        {
            var Q0;
            Q0=makeQuery(id+"F1.opExtrude","CAP_EDGE",EDGE,{"disambiguationData":[OSD([sQuery(id+"F0.wireOp",EDGE,"E0")])],"isStart":true});
            var Q1;
            Q1=makeQuery(id+"F8.opExtrude","TWEAK_EDGE",EDGE,{"derivedFrom":[makeQuery(id+"F4.imprint","IMPRINT",EDGE,{"derivedFrom":sQuery(id+"F4.wireOp",EDGE,"E9")}),makeQuery(id+"F4.imprint","IMPRINT",EDGE,{"derivedFrom":sQuery(id+"F4.wireOp",EDGE,"E13")})]});
            var Q2;
            Q2=makeQuery(id+"F7.opLoft","MID_CAP_EDGE",EDGE,{"disambiguationData":[OSD([sQuery(id+"F5.wireOp",EDGE,"E14"),sQuery(id+"F6.wireOp",EDGE,"E16")])],"capPos":1.0});
            var Q3;
            Q3=makeQuery(id+"F8.opExtrude","TWEAK_EDGE",EDGE,{"derivedFrom":[makeQuery(id+"F4.imprint","IMPRINT",EDGE,{"derivedFrom":sQuery(id+"F4.wireOp",EDGE,"E10")}),makeQuery(id+"F4.imprint","IMPRINT",EDGE,{"derivedFrom":sQuery(id+"F4.wireOp",EDGE,"E13")})]});
            var Q4;
            Q4=makeQuery(id+"F10.opExtrude","CAP_EDGE",EDGE,{"disambiguationData":[OSD([sQuery(id+"F9.wireOp",EDGE,"E17")])],"isStart":false});
            fillet(context, id + "F12", {"entities" : qUnion([Q0, Q1, Q2, Q3, Q4]), "radius" : 1 * mm, "tangentPropagation" : true, "allowEdgeOverflow" : false});
        }
    });
